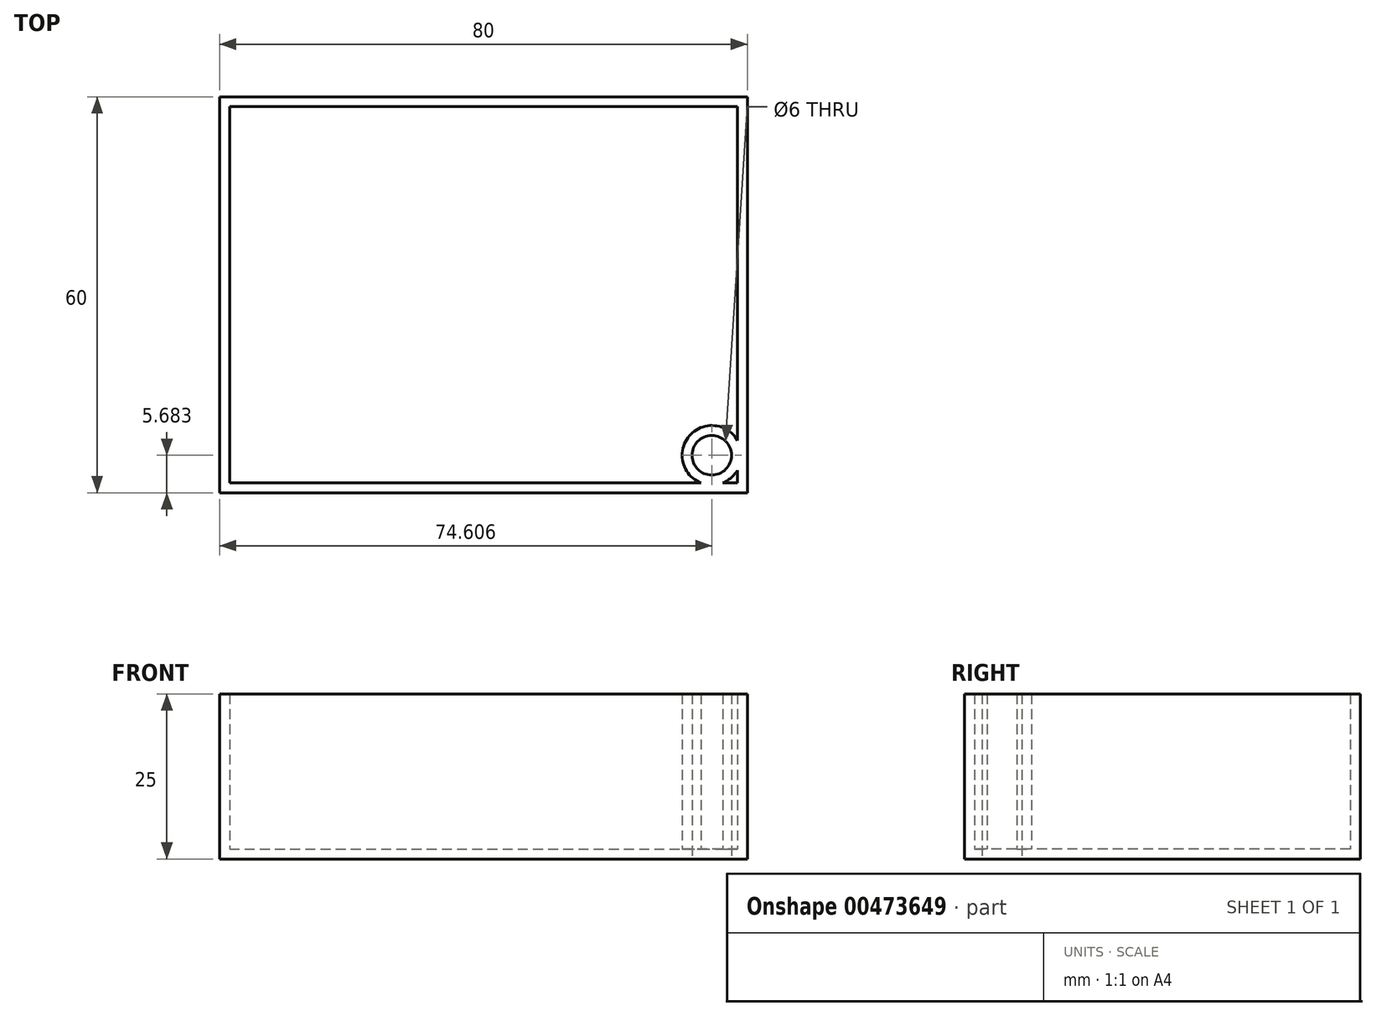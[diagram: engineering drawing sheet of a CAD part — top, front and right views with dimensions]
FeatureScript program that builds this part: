
annotation { "Feature Type Name" : "Feature", "Feature Type Description" : "" }
export const myFeature = defineFeature(function(context is Context, id is Id, definition is map)
    precondition{}
    {
        {
            var Q0;
            Q0=qCreatedBy(makeId("Top.planeOp"),FACE);
            var sketch = newSketch(context, id + "F0", { "sketchPlane" : qUnion([Q0])});
            skLineSegment(sketch, "E0.bottom", {"start": v(-24.75, 40.72) * mm, "end": v(55.25, 40.72) * mm});
            skLineSegment(sketch, "E0.top", {"start": v(-24.75, -19.28) * mm, "end": v(55.25, -19.28) * mm});
            skLineSegment(sketch, "E0.left", {"start": v(-24.75, 40.72) * mm, "end": v(-24.75, -19.28) * mm});
            skLineSegment(sketch, "E0.right", {"start": v(55.25, 40.72) * mm, "end": v(55.25, -19.28) * mm});
            skCircle(sketch, "E1", {"center": v(49.86, -13.6) * mm, "radius": 3 * mm});
            skSolve(sketch);
        }
        {
            var Q0;
            Q0 = qSketchRegion(id + "F0", true);
            extrude(context, id + "F1", {"entities" : qUnion([Q0]), "depth" : 25 * mm});
        }
        {
            var Q0;
            Q0=makeQuery(id+"F1.opExtrude","CAP_FACE",FACE,{"disambiguationData":[OSD([sQuery(id+"F0.wireOp",EDGE,"E0.bottom"),sQuery(id+"F0.wireOp",EDGE,"E0.top"),sQuery(id+"F0.wireOp",EDGE,"E0.left"),sQuery(id+"F0.wireOp",EDGE,"E0.right")])],"isStart":false});
            shell(context, id + "F2", {"entities" : qUnion([Q0]), "thickness" : 1.5 * mm});
        }
    });
